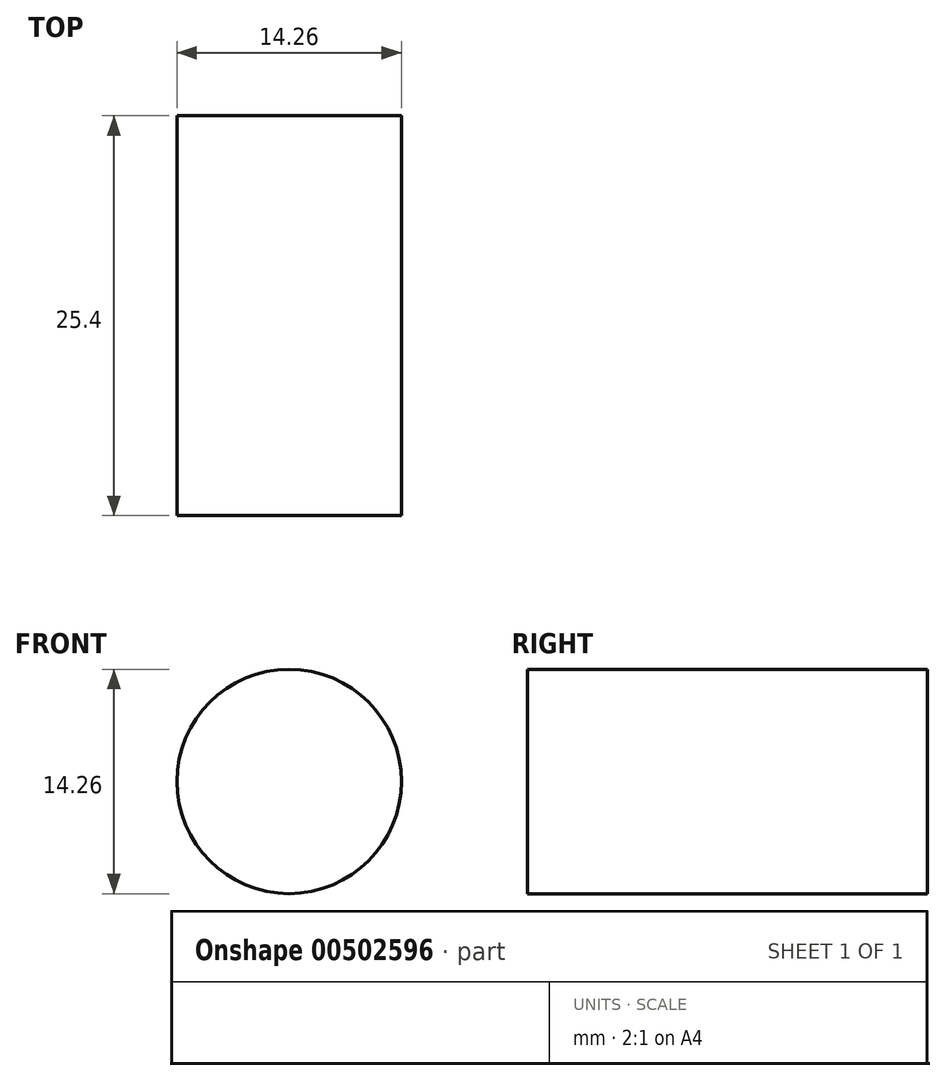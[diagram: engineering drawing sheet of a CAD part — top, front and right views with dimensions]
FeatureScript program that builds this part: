
annotation { "Feature Type Name" : "Feature", "Feature Type Description" : "" }
export const myFeature = defineFeature(function(context is Context, id is Id, definition is map)
    precondition{}
    {
        {
            var Q0;
            Q0=qCreatedBy(makeId("Front.planeOp"),FACE);
            var sketch = newSketch(context, id + "F0", { "sketchPlane" : qUnion([Q0])});
            skCircle(sketch, "E0", {"center": v(0, 0) * mm, "radius": 7.13 * mm});
            skSolve(sketch);
        }
        {
            var Q0;
            Q0=makeQuery(id+"F0.imprint","IMPRINT",FACE,{"disambiguationData":[TD([[makeQuery(id+"F0.imprint","IMPRINT",EDGE,{"derivedFrom":sQuery(id+"F0.wireOp",EDGE,"E0")}),1.0]])]});
            extrude(context, id + "F1", {"entities" : qUnion([Q0]), "depth" : 25.4 * mm});
        }
    });
